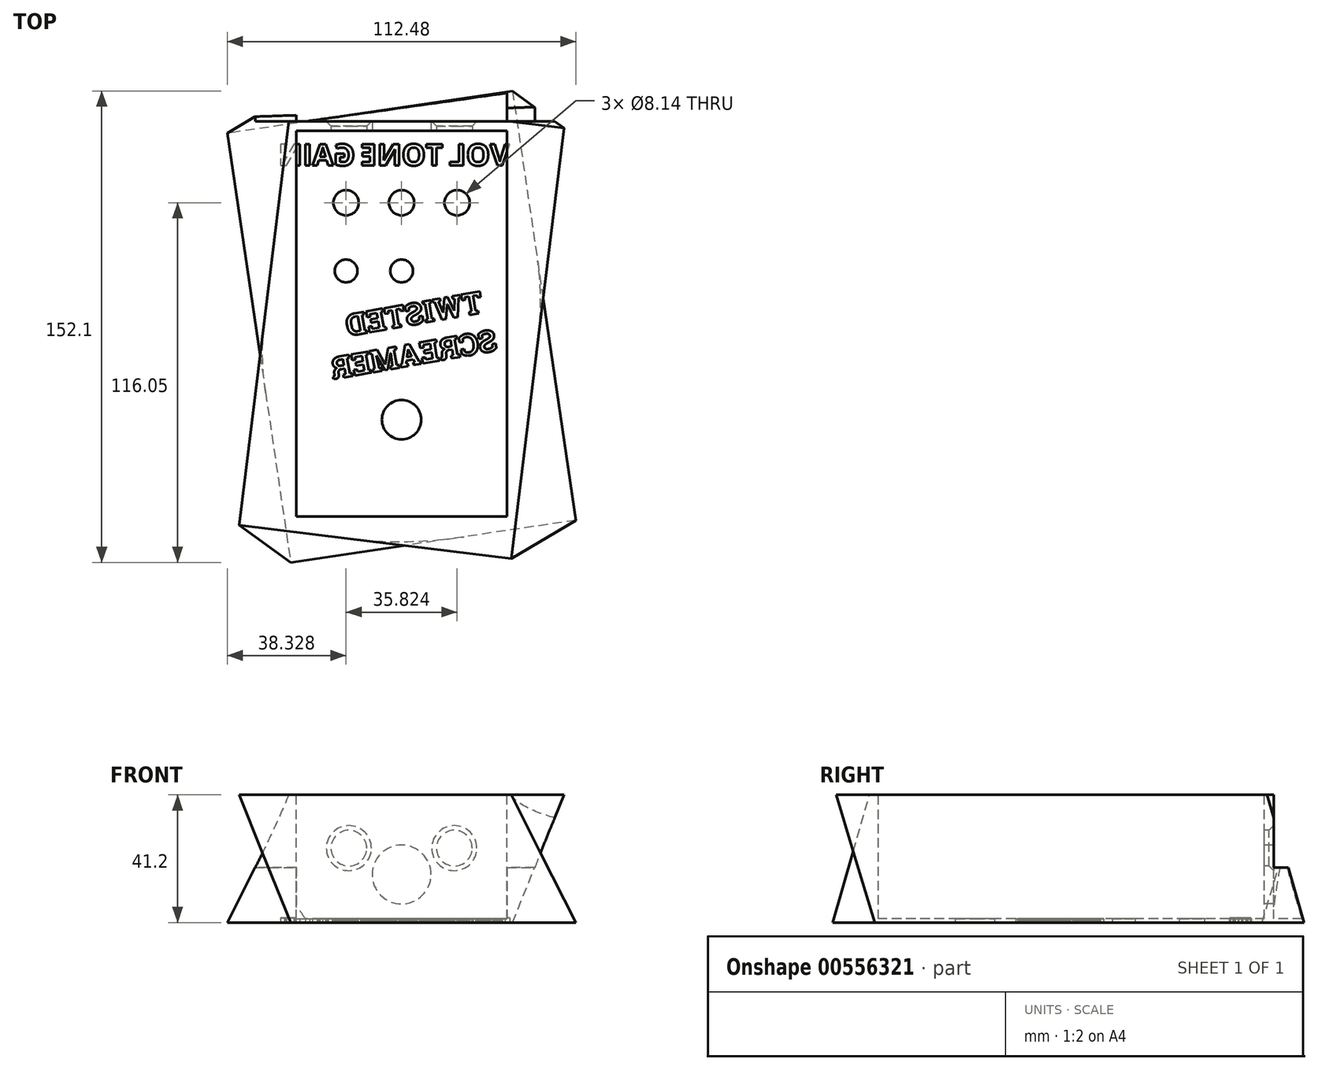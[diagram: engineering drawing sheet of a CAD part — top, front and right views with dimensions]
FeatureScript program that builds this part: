
annotation { "Feature Type Name" : "Feature", "Feature Type Description" : "" }
export const myFeature = defineFeature(function(context is Context, id is Id, definition is map)
    precondition{}
    {
        {
            var Q0;
            Q0=qCreatedBy(makeId("Top.planeOp"),FACE);
            var sketch = newSketch(context, id + "F0", { "sketchPlane" : qUnion([Q0])});
            skLineSegment(sketch, "E0.bottom", {"start": v(-36.5, 64) * mm, "end": v(36.5, 64) * mm});
            skLineSegment(sketch, "E0.top", {"start": v(-36.5, -64) * mm, "end": v(36.5, -64) * mm});
            skLineSegment(sketch, "E0.left", {"start": v(-36.5, 64) * mm, "end": v(-36.5, -64) * mm});
            skLineSegment(sketch, "E0.right", {"start": v(36.5, 64) * mm, "end": v(36.5, -64) * mm});
            skSolve(sketch);
        }
        {
            var Q0;
            Q0=makeQuery(id+"F0.imprint","IMPRINT",FACE,{"disambiguationData":[TD([[makeQuery(id+"F0.imprint","IMPRINT",EDGE,{"derivedFrom":sQuery(id+"F0.wireOp",EDGE,"E0.bottom")}),-1.0]])]});
            extrude(context, id + "F1", {"entities" : qUnion([Q0]), "depth" : 41.2 * mm, "offsetDistance" : 25 * mm});
        }
        {
            var Q0;
            {var subQ0=sQuery(id+"F0.wireOp",EDGE,"E0.bottom");var subQ1=sQuery(id+"F0.wireOp",EDGE,"E0.left");var subQ2=sQuery(id+"F0.wireOp",EDGE,"E0.top");var subQ3=sQuery(id+"F0.wireOp",EDGE,"E0.right");Q0=makeQuery(id+"F16.boolean.opBoolean","SPLIT",FACE,{"disambiguationData":[TD([makeQuery(id+"F1.opExtrude","SWEPT_FACE",FACE,{"disambiguationData":[OSD([subQ0])]})])],"derivedFrom":makeQuery(id+"F1.opExtrude","CAP_FACE",FACE,{"disambiguationData":[OSD([subQ0,subQ2,subQ1,subQ3])],"isStart":true})});}
            var sketch = newSketch(context, id + "F2", { "sketchPlane" : qUnion([Q0])});
            skLineSegment(sketch, "E1.bottom", {"start": v(35.76, -75.05) * mm, "end": v(-56.24, -61.45) * mm});
            skLineSegment(sketch, "E1.top", {"start": v(56.24, 63.45) * mm, "end": v(-35.76, 77.05) * mm});
            skLineSegment(sketch, "E1.left", {"start": v(35.76, -75.05) * mm, "end": v(56.24, 63.45) * mm});
            skLineSegment(sketch, "E1.right", {"start": v(-56.24, -61.45) * mm, "end": v(-35.76, 77.05) * mm});
            skPoint(sketch, "E1.middle", {"position": v(0, 1) * mm});
            skSolve(sketch);
        }
        {
            var Q0;
            Q0=makeQuery(id+"F1.opExtrude","CAP_FACE",FACE,{"disambiguationData":[OSD([sQuery(id+"F0.wireOp",EDGE,"E0.bottom"),sQuery(id+"F0.wireOp",EDGE,"E0.top"),sQuery(id+"F0.wireOp",EDGE,"E0.left"),sQuery(id+"F0.wireOp",EDGE,"E0.right")])],"isStart":false});
            var sketch = newSketch(context, id + "F3", { "sketchPlane" : qUnion([Q0])});
            skLineSegment(sketch, "E2.bottom", {"start": v(-35.35, 73.87) * mm, "end": v(52.41, 63.1) * mm});
            skLineSegment(sketch, "E2.top", {"start": v(-52.41, -65.1) * mm, "end": v(35.35, -75.87) * mm});
            skLineSegment(sketch, "E2.left", {"start": v(-35.35, 73.87) * mm, "end": v(-52.41, -65.1) * mm});
            skLineSegment(sketch, "E2.right", {"start": v(52.41, 63.1) * mm, "end": v(35.35, -75.87) * mm});
            skPoint(sketch, "E2.middle", {"position": v(0, -1) * mm});
            skSolve(sketch);
        }
        {
            var Q1;
            Q1=qSketchRegion(id+"F2",true);
            var Q2;
            Q2=qSketchRegion(id+"F3",true);
            var Q3;
            Q3=sQuery(id+"F2.wireOp",VERTEX,"E1.left.start");
            var Q4;
            Q4=sQuery(id+"F3.wireOp",VERTEX,"E2.right.start");
            loft(context, id + "F4", {"operationType" : NewBodyOperationType.ADD, "sheetProfilesArray" : [{ "sheetProfileEntities" : qUnion([Q1]) }, { "sheetProfileEntities" : qUnion([Q2]) }], "matchConnections" : true, "connections" : [{ "connectionEntities" : qUnion([Q3, Q4]), "connectionEdgeQueries" : qUnion([]), "connectionEdgeParameters" : [] }]});
        }
        {
            var Q0;
            Q0=makeQuery(id+"F1.opExtrude","CAP_FACE",FACE,{"disambiguationData":[OSD([sQuery(id+"F0.wireOp",EDGE,"E0.bottom"),sQuery(id+"F0.wireOp",EDGE,"E0.top"),sQuery(id+"F0.wireOp",EDGE,"E0.left"),sQuery(id+"F0.wireOp",EDGE,"E0.right")])],"isStart":false});
            var sketch = newSketch(context, id + "F5", { "sketchPlane" : qUnion([Q0])});
            skLineSegment(sketch, "E3.bottom", {"start": v(-34, 62.25) * mm, "end": v(34, 62.25) * mm});
            skLineSegment(sketch, "E3.top", {"start": v(-34, -62.25) * mm, "end": v(34, -62.25) * mm});
            skLineSegment(sketch, "E3.left", {"start": v(-34, 62.25) * mm, "end": v(-34, -62.25) * mm});
            skLineSegment(sketch, "E3.right", {"start": v(34, 62.25) * mm, "end": v(34, -62.25) * mm});
            skSolve(sketch);
        }
        {
            var Q0;
            Q0=makeQuery(id+"F5.imprint","IMPRINT",FACE,{"disambiguationData":[TD([[makeQuery(id+"F5.imprint","IMPRINT",EDGE,{"derivedFrom":sQuery(id+"F5.wireOp",EDGE,"E3.bottom")}),-1.0]])]});
            extrude(context, id + "F6", {"entities" : qUnion([Q0]), "operationType" : NewBodyOperationType.REMOVE, "oppositeDirection" : true, "depth" : 40 * mm, "offsetDistance" : 25 * mm});
        }
        {
            var Q0;
            Q0=makeQuery(id+"F6.boolean.opBoolean","COPY",FACE,{"derivedFrom":makeQuery(id+"F6.opExtrude","CAP_FACE",FACE,{"disambiguationData":[OSD([sQuery(id+"F5.wireOp",EDGE,"E3.bottom"),sQuery(id+"F5.wireOp",EDGE,"E3.top"),sQuery(id+"F5.wireOp",EDGE,"E3.left"),sQuery(id+"F5.wireOp",EDGE,"E3.right")])],"isStart":false})});
            var sketch = newSketch(context, id + "F7", { "sketchPlane" : qUnion([Q0])});
            skCircle(sketch, "E4", {"center": v(-17.91, 39) * mm, "radius": 4.07 * mm});
            skCircle(sketch, "E5", {"center": v(0, 39) * mm, "radius": 4.07 * mm});
            skCircle(sketch, "E6", {"center": v(17.91, 39) * mm, "radius": 4.07 * mm});
            skCircle(sketch, "E7", {"center": v(0, -31) * mm, "radius": 6.35 * mm});
            skLineSegment(sketch, "E8", {"start": v(17.91, 39) * mm, "end": v(0, 39) * mm, "construction": true});
            skLineSegment(sketch, "E9", {"start": v(8.96, 39) * mm, "end": v(8.96, 15.16) * mm, "construction": true});
            skCircle(sketch, "E10", {"center": v(8.96, 17) * mm, "radius": 3.67 * mm, "construction": true});
            skCircle(sketch, "E11", {"center": v(0, -1) * mm, "radius": 3.67 * mm, "construction": true});
            skCircle(sketch, "E12", {"center": v(0, 17) * mm, "radius": 3.67 * mm});
            skCircle(sketch, "E13", {"center": v(-17.91, 17) * mm, "radius": 3.67 * mm});
            skSolve(sketch);
        }
        {
            var Q0;
            Q0=qSketchRegion(id+"F7",true);
            extrude(context, id + "F8", {"entities" : qUnion([Q0]), "operationType" : NewBodyOperationType.REMOVE, "oppositeDirection" : true, "depth" : 25 * mm, "offsetDistance" : 25 * mm});
        }
        {
            var Q0;
            Q0=makeQuery(id+"F6.boolean.opBoolean","COPY",FACE,{"derivedFrom":makeQuery(id+"F6.opExtrude","SWEPT_FACE",FACE,{"disambiguationData":[OSD([sQuery(id+"F5.wireOp",EDGE,"E3.bottom")])]})});
            cPlane(context, id + "F9", {"entities" : qUnion([Q0]), "cplaneType" : CPlaneType.OFFSET, "offset" : 3 * mm, "oppositeDirection" : true, "width" : 150 * mm, "height" : 150 * mm});
        }
        {
            var Q0;
            Q0=qCreatedBy(id+"F9.planeOp",FACE);
            var sketch = newSketch(context, id + "F10", { "sketchPlane" : qUnion([Q0])});
            skCircle(sketch, "E14", {"center": v(0, 15.5) * mm, "radius": 9.5 * mm});
            skCircle(sketch, "E15", {"center": v(17, 24) * mm, "radius": 5.76 * mm});
            skCircle(sketch, "E16", {"center": v(-17, 24) * mm, "radius": 5.76 * mm});
            skSolve(sketch);
        }
        {
            var Q0;
            Q0=qSketchRegion(id+"F10",true);
            extrude(context, id + "F11", {"entities" : qUnion([Q0]), "operationType" : NewBodyOperationType.REMOVE, "endBound" : BoundingType.SYMMETRIC, "oppositeDirection" : true, "depth" : 30 * mm, "offsetDistance" : 25 * mm});
        }
        {
            var Q0;
            Q0=qCreatedBy(id+"F9.planeOp",FACE);
            var sketch = newSketch(context, id + "F12", { "sketchPlane" : qUnion([Q0])});
            skLineSegment(sketch, "E17.0", {"start": v(-34, 1.2) * mm, "end": v(-34, 41.2) * mm});
            skLineSegment(sketch, "E18.0", {"start": v(-34, 1.2) * mm, "end": v(34, 1.2) * mm});
            skLineSegment(sketch, "E19.0", {"start": v(34, 1.2) * mm, "end": v(34, 41.2) * mm});
            skLineSegment(sketch, "E20.0", {"start": v(-34, 41.2) * mm, "end": v(34, 41.2) * mm});
            skSolve(sketch);
        }
        {
            var Q0;
            Q0=qSketchRegion(id+"F12",true);
            extrude(context, id + "F13", {"entities" : qUnion([Q0]), "operationType" : NewBodyOperationType.REMOVE, "oppositeDirection" : true, "depth" : 25 * mm, "offsetDistance" : 25 * mm});
        }
        {
            var Q0;
            Q0=qCreatedBy(makeId("Front.planeOp"),FACE);
            cPlane(context, id + "F14", {"entities" : qUnion([Q0]), "cplaneType" : CPlaneType.OFFSET, "offset" : 38 * mm, "width" : 150 * mm, "height" : 150 * mm});
        }
        {
            var Q0;
            Q0=makeQuery(id+"F1.opExtrude","CAP_FACE",FACE,{"disambiguationData":[OSD([sQuery(id+"F0.wireOp",EDGE,"E0.bottom"),sQuery(id+"F0.wireOp",EDGE,"E0.top"),sQuery(id+"F0.wireOp",EDGE,"E0.left"),sQuery(id+"F0.wireOp",EDGE,"E0.right")])],"isStart":true});
            var sketch = newSketch(context, id + "F15", { "sketchPlane" : qUnion([Q0])});
            skText(sketch, "E21", { "text": "VOL", "fontName": "OpenSans-Bold.ttf"});
            skText(sketch, "E22", { "text": "TONE", "fontName": "OpenSans-Bold.ttf"});
            skText(sketch, "E23", { "text": "GAIN", "fontName": "OpenSans-Bold.ttf"});
            skText(sketch, "E24", { "text": " TWISTED \nSCREAMER", "fontName": "RobotoSlab-Bold.ttf"});
            const initialGuessF15  = {"E21": [0.03485, -0.051, -1, 0, 0.007], "E22": [0.01339, -0.051, -1, 0, 0.007], "E23": [-0.015, -0.051, -1, 0, 0.007], "E24": [0.02894, -0.00406, -0.9848, 0.17365, 0.007]};
            skSetInitialGuess(sketch, initialGuessF15);
            skSolve(sketch);
        }
        {
            var Q0;
            Q0=qSketchRegion(id+"F15",true);
            extrude(context, id + "F16", {"entities" : qUnion([Q0]), "operationType" : NewBodyOperationType.REMOVE, "oppositeDirection" : true, "depth" : 1.5 * mm, "offsetDistance" : 25 * mm});
        }
        {
            var Q0;
            Q0=makeQuery(id+"F13.boolean.opBoolean","COPY",FACE,{"derivedFrom":makeQuery(id+"F13.opExtrude","CAP_FACE",FACE,{"disambiguationData":[OSD([sQuery(id+"F12.wireOp",EDGE,"E17.0"),sQuery(id+"F12.wireOp",EDGE,"E18.0"),sQuery(id+"F12.wireOp",EDGE,"E19.0"),sQuery(id+"F12.wireOp",EDGE,"E20.0")])],"isStart":true})});
            var sketch = newSketch(context, id + "F17", { "sketchPlane" : qUnion([Q0])});
            skLineSegment(sketch, "E25", {"start": v(75, 17.76) * mm, "end": v(-75, 17.76) * mm});
            skLineSegment(sketch, "E26", {"start": v(-75, 17.76) * mm, "end": v(-75, 44.5) * mm});
            skLineSegment(sketch, "E27", {"start": v(-75, 44.5) * mm, "end": v(75, 44.5) * mm});
            skLineSegment(sketch, "E28", {"start": v(75, 44.5) * mm, "end": v(75, 17.76) * mm});
            skSolve(sketch);
        }
        {
            var Q0;
            Q0=qSketchRegion(id+"F17",true);
            extrude(context, id + "F18", {"entities" : qUnion([Q0]), "operationType" : NewBodyOperationType.REMOVE, "depth" : 15 * mm, "offsetDistance" : 25 * mm});
        }
        {
            var Q0;
            Q0=makeQuery(id+"F13.boolean.opBoolean","INTERSECT",EDGE,{"derivedFrom":[makeQuery(id+"F11.boolean.opBoolean","COPY",FACE,{"derivedFrom":makeQuery(id+"F11.opExtrude","SWEPT_FACE",FACE,{"disambiguationData":[OSD([sQuery(id+"F10.wireOp",EDGE,"E16")])]})}),makeQuery(id+"F13.opExtrude","CAP_FACE",FACE,{"disambiguationData":[OSD([sQuery(id+"F12.wireOp",EDGE,"E17.0"),sQuery(id+"F12.wireOp",EDGE,"E18.0"),sQuery(id+"F12.wireOp",EDGE,"E19.0"),sQuery(id+"F12.wireOp",EDGE,"E20.0")])],"isStart":true})]});
            var Q1;
            Q1=makeQuery(id+"F13.boolean.opBoolean","INTERSECT",EDGE,{"derivedFrom":[makeQuery(id+"F11.boolean.opBoolean","COPY",FACE,{"derivedFrom":makeQuery(id+"F11.opExtrude","SWEPT_FACE",FACE,{"disambiguationData":[OSD([sQuery(id+"F10.wireOp",EDGE,"E15")])]})}),makeQuery(id+"F13.opExtrude","CAP_FACE",FACE,{"disambiguationData":[OSD([sQuery(id+"F12.wireOp",EDGE,"E17.0"),sQuery(id+"F12.wireOp",EDGE,"E18.0"),sQuery(id+"F12.wireOp",EDGE,"E19.0"),sQuery(id+"F12.wireOp",EDGE,"E20.0")])],"isStart":true})]});
            chamfer(context, id + "F19", {"entities" : qUnion([Q0, Q1]), "width" : 1.5 * mm, "tangentPropagation" : true});
        }
    });
